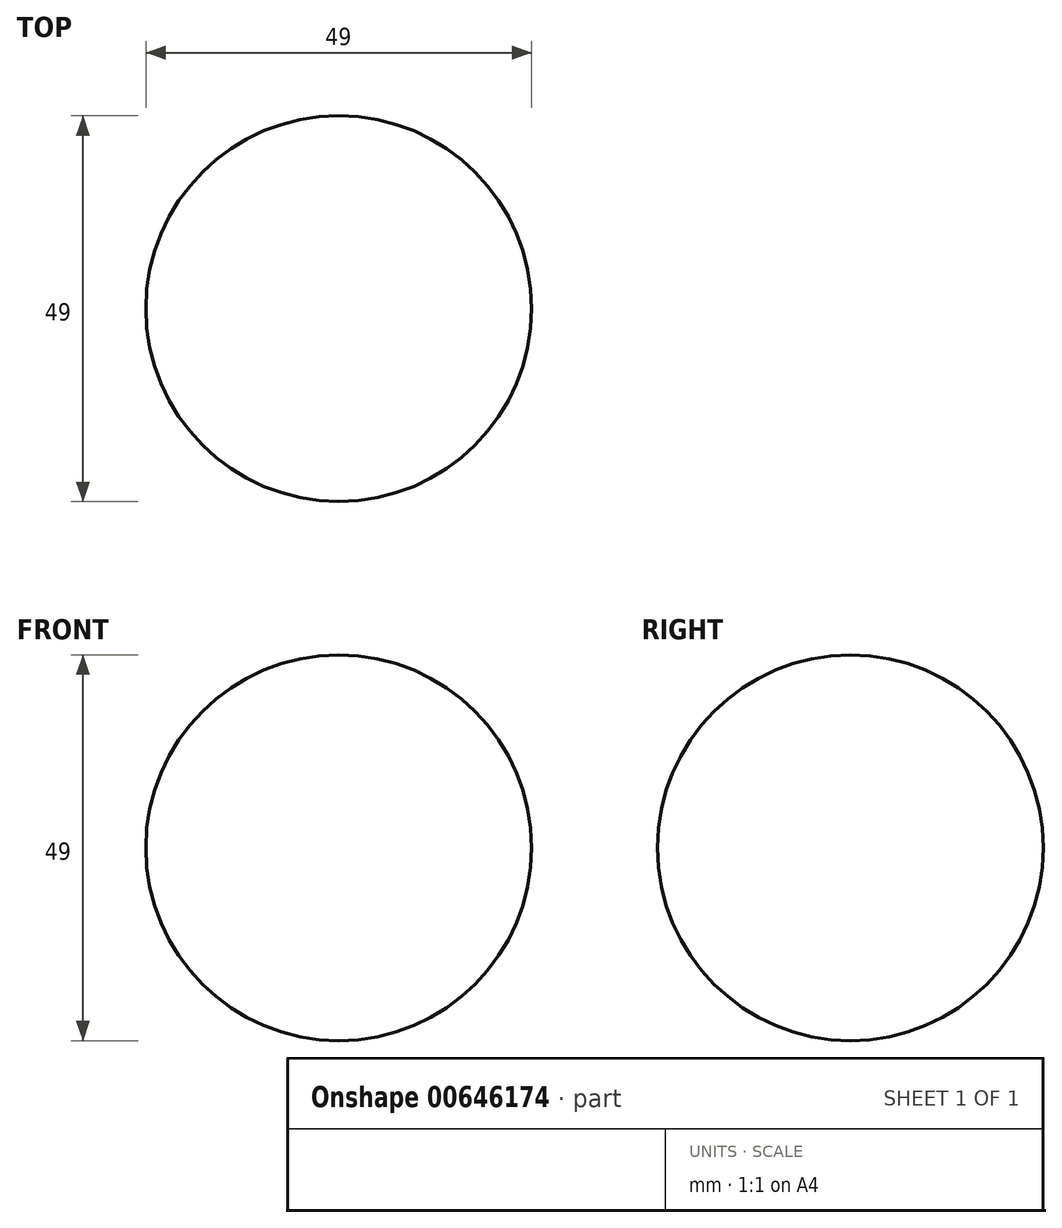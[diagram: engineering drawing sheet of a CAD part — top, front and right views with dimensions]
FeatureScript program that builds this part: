
annotation { "Feature Type Name" : "Feature", "Feature Type Description" : "" }
export const myFeature = defineFeature(function(context is Context, id is Id, definition is map)
    precondition{}
    {
        {
            var Q0;
            Q0=qCreatedBy(makeId("Top.planeOp"),FACE);
            var sketch = newSketch(context, id + "F0", { "sketchPlane" : qUnion([Q0])});
            skLineSegment(sketch, "E0", {"start": v(0, 0) * mm, "end": v(-49, 0) * mm});
            skArc(sketch, "E1", {"start": v(-49, 0) * mm, "mid": v(-24.5, -24.5) * mm, "end": v(0, 0) * mm});
            skSolve(sketch);
        }
        {
            var Q0;
            Q0=makeQuery(id+"F0.imprint","IMPRINT",FACE,{"disambiguationData":[TD([[makeQuery(id+"F0.imprint","IMPRINT",EDGE,{"derivedFrom":sQuery(id+"F0.wireOp",EDGE,"E0")}),1.0]])]});
            var Q1;
            Q1=sQuery(id+"F0.wireOp",EDGE,"E0");
            revolve(context, id + "F1", {"entities" : qUnion([Q0]), "axis" : qUnion([Q1]), "revolveType" : RevolveType.FULL});
        }
    });
